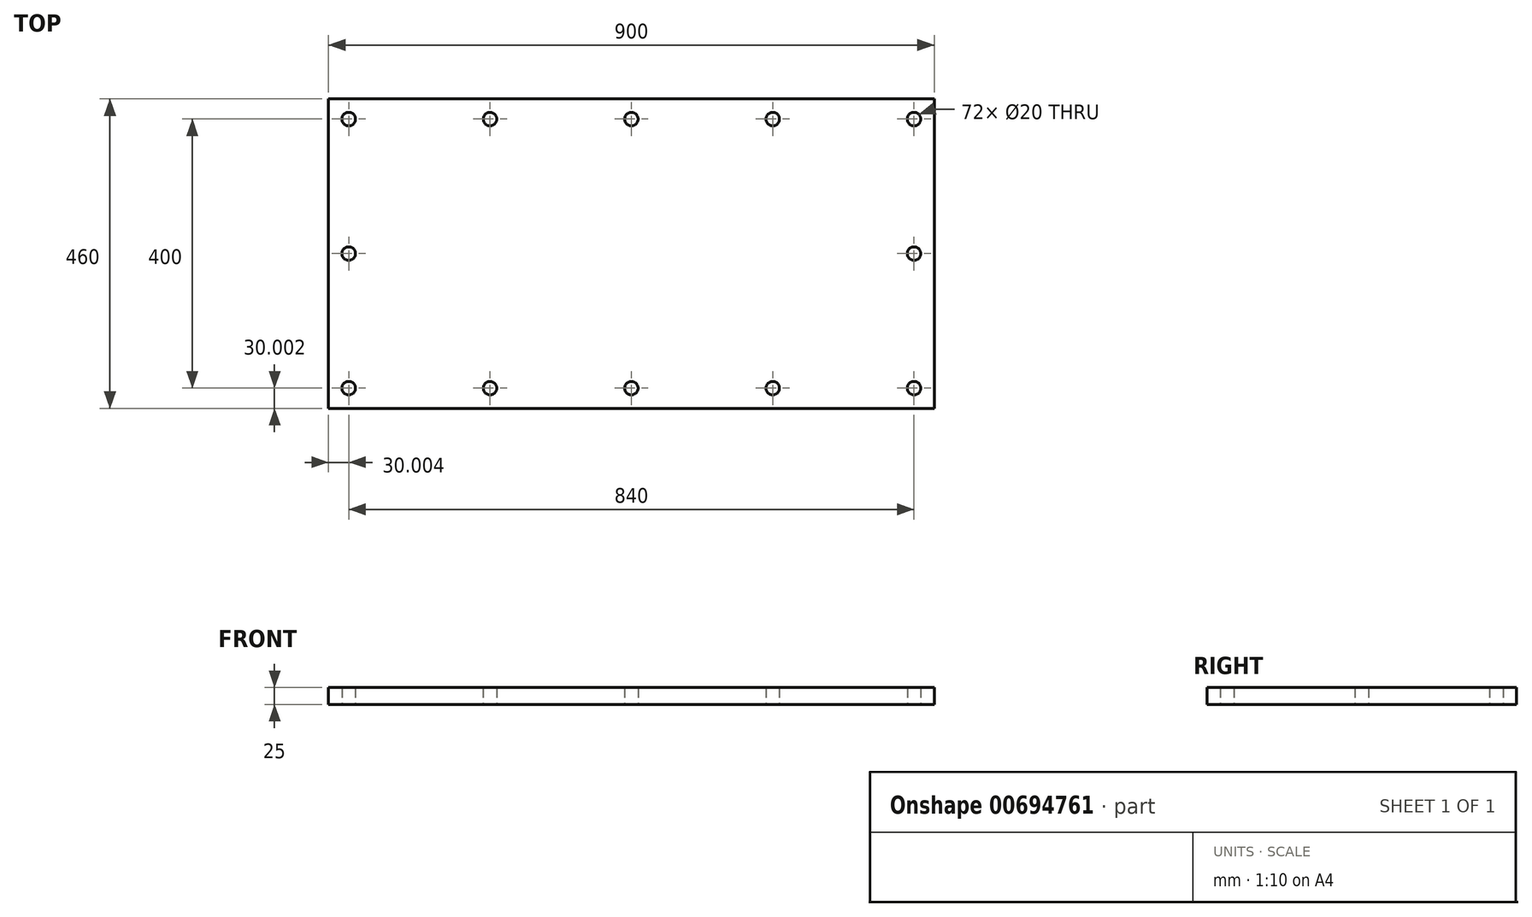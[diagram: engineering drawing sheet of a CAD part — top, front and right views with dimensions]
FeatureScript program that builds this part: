
annotation { "Feature Type Name" : "Feature", "Feature Type Description" : "" }
export const myFeature = defineFeature(function(context is Context, id is Id, definition is map)
    precondition{}
    {
        {
            var Q0;
            Q0=qCreatedBy(makeId("Top.planeOp"),FACE);
            var sketch = newSketch(context, id + "F0", { "sketchPlane" : qUnion([Q0])});
            skLineSegment(sketch, "E0.bottom", {"start": v(-432.47, 216.12) * mm, "end": v(467.53, 216.12) * mm});
            skLineSegment(sketch, "E0.top", {"start": v(-432.47, -243.88) * mm, "end": v(467.53, -243.88) * mm});
            skLineSegment(sketch, "E0.left", {"start": v(-432.47, 216.12) * mm, "end": v(-432.47, -243.88) * mm});
            skLineSegment(sketch, "E0.right", {"start": v(467.53, 216.12) * mm, "end": v(467.53, -243.88) * mm});
            skCircle(sketch, "E1", {"center": v(-402.47, 186.12) * mm, "radius": 10 * mm});
            skCircle(sketch, "E2.0.1.0", {"center": v(-402.47, -13.88) * mm, "radius": 10 * mm});
            skCircle(sketch, "E2.0.2.0", {"center": v(-402.47, -213.88) * mm, "radius": 10 * mm});
            skCircle(sketch, "E2.1.0.0", {"center": v(-192.47, 186.12) * mm, "radius": 10 * mm});
            skCircle(sketch, "E2.1.2.0", {"center": v(-192.47, -213.88) * mm, "radius": 10 * mm});
            skCircle(sketch, "E2.2.0.0", {"center": v(17.53, 186.12) * mm, "radius": 10 * mm});
            skCircle(sketch, "E2.2.2.0", {"center": v(17.53, -213.88) * mm, "radius": 10 * mm});
            skCircle(sketch, "E2.3.0.0", {"center": v(227.53, 186.12) * mm, "radius": 10 * mm});
            skCircle(sketch, "E2.3.2.0", {"center": v(227.53, -213.88) * mm, "radius": 10 * mm});
            skCircle(sketch, "E2.4.0.0", {"center": v(437.53, 186.12) * mm, "radius": 10 * mm});
            skCircle(sketch, "E2.4.1.0", {"center": v(437.53, -13.88) * mm, "radius": 10 * mm});
            skCircle(sketch, "E2.4.2.0", {"center": v(437.53, -213.88) * mm, "radius": 10 * mm});
            skLineSegment(sketch, "E2.direction1", {"start": v(-402.47, 186.12) * mm, "end": v(-192.47, 186.12) * mm, "construction": true});
            skLineSegment(sketch, "E2.direction2", {"start": v(-402.47, 186.12) * mm, "end": v(-402.47, -13.88) * mm, "construction": true});
            skSolve(sketch);
        }
        {
            var Q0;
            Q0=makeQuery(id+"F0.imprint","IMPRINT",FACE,{"disambiguationData":[TD([[makeQuery(id+"F0.imprint","IMPRINT",EDGE,{"derivedFrom":sQuery(id+"F0.wireOp",EDGE,"E0.bottom")}),-1.0]])]});
            extrude(context, id + "F1", {"entities" : qUnion([Q0]), "depth" : 25 * mm, "offsetDistance" : 25 * mm});
        }
    });
